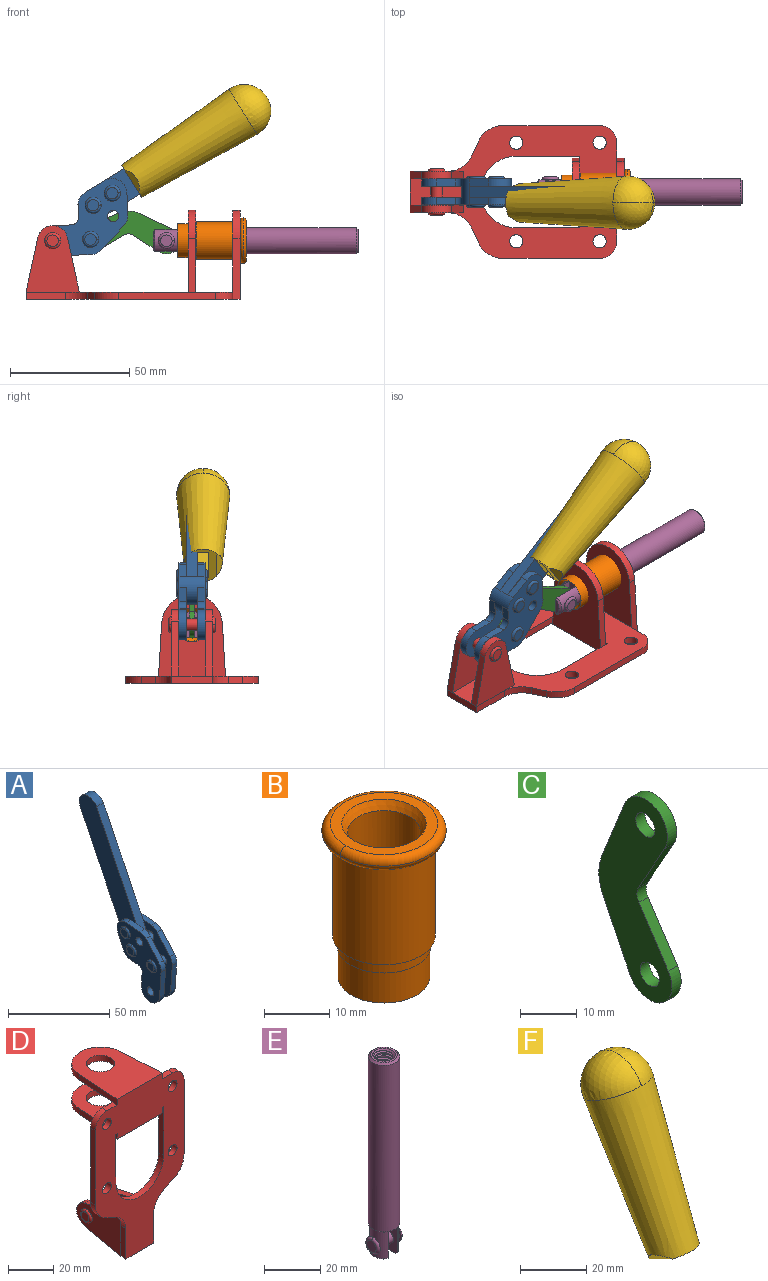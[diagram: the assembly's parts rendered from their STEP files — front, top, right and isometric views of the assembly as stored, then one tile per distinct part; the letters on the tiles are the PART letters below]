
ASSEMBLY  parts=6 mates=6
PART A: 59 faces, bbox 12.9x60.2x99.6 mm
  f0: torus R=2.39mm, axis (-1,0,0), area 14.9mm2, adj f20,f43,f51
  f1: torus R=2.39mm, axis (-1,0,0), area 14.9mm2, adj f19,f42,f51
  f2: torus R=2.39mm, axis (-1,0,0), area 14.9mm2, adj f18,f35,f51
  f3: torus R=2.39mm, axis (-1,0,0), area 14.9mm2, adj f14,f17,f23
  f4: torus R=2.39mm, axis (-1,0,0), area 14.9mm2, adj f13,f16,f23
  f5: torus R=2.39mm, axis (-1,0,0), area 14.9mm2, adj f12,f15,f23
  f6: cylinder r=2.39mm len=4.78mm, axis (1,0,0), area 46.5mm2, adj f48,f50,f51
  f7: cylinder r=2.39mm len=4.78mm, axis (1,0,0), area 46.5mm2, adj f50,f51
  f8: cylinder r=6.35mm len=12.68mm, axis (1,0,0), area 61.8mm2, adj f38,f39,f50,f51
  f9: cylinder r=2.39mm len=4.78mm, axis (-1,0,0), area 70.5mm2, adj f46,f50
  f10: cylinder r=2.39mm len=4.78mm, axis (-1,0,0), area 46.5mm2, adj f23,f45,f46
  f11: cylinder r=2.39mm len=4.78mm, axis (-1,0,0), area 46.5mm2, adj f23,f46
  f12: plane 4.78x4.78mm, normal (1,0,0), area 17.9mm2, adj f5,f15
  f13: plane 4.78x4.78mm, normal (1,0,0), area 17.9mm2, adj f4,f16
  f14: plane 4.78x4.78mm, normal (1,0,0), area 17.9mm2, adj f3,f17
  f15: torus R=2.39mm, axis (-1,0,0), area 14.9mm2, adj f5,f12,f23
  f16: torus R=2.39mm, axis (-1,0,0), area 14.9mm2, adj f4,f13,f23
  f17: torus R=2.39mm, axis (-1,0,0), area 14.9mm2, adj f3,f14,f23
  f18: plane 4.78x4.78mm, normal (-1,0,0), area 17.9mm2, adj f2,f35
  f19: plane 4.78x4.78mm, normal (-1,0,0), area 17.9mm2, adj f1,f42
  f20: plane 4.78x4.78mm, normal (-1,0,0), area 17.9mm2, adj f0,f43
  f21: plane 2.26x0.2mm, normal (1,0,0), area 0.2mm2, adj f31,f44
  f22: plane 2.26x0.2mm, normal (-1,0,0), area 0.2mm2, adj f41,f44
  f23: plane 39.37x30.77mm, normal (1,0,0), area 565.5mm2, adj f3,f4,f5,f10,f11,f15,f16,f17
  f24: cylinder r=6.1mm len=4.15mm, axis (-1,0,0), area 14.7mm2, adj f23,f25,f32,f46
  f25: plane 10.25x9.01mm, normal (0,-0.75,0.66), area 42.3mm2, adj f23,f24,f26,f46
  f26: cylinder r=6.35mm len=4.64mm, axis (-1,0,0), area 15.6mm2, adj f23,f25,f27,f46
  f27: plane 15.84x3.1mm, normal (0,-1,-0.07), area 49.2mm2, adj f23,f26,f28,f46
  f28: cylinder r=6.35mm len=12.68mm, axis (-1,0,0), area 61.8mm2, adj f23,f27,f29,f46
  f29: plane 8.11x3.1mm, normal (0,1,0.07), area 25.2mm2, adj f23,f28,f30,f46
  f30: cylinder r=3.05mm len=3.25mm, axis (-1,0,0), area 14.8mm2, adj f23,f29,f31,f46
  f31: plane 5.99x3.1mm, normal (0,0.07,-1), area 18.6mm2, adj f21,f23,f30,f44,f46
  f32: plane 9.5x3.1mm, normal (0,-0.07,1), area 29.5mm2, adj f23,f24,f33,f46,f47
  f33: cylinder r=6.1mm len=8.63mm, axis (-1,0,0), area 39.1mm2, adj f23,f32,f34,f47
  f34: plane 8.65x3.96mm, normal (0,0.91,-0.42), area 29.5mm2, adj f23,f33,f44,f47
  f35: torus R=2.39mm, axis (-1,0,0), area 14.9mm2, adj f2,f18,f51
  f36: plane 10.25x9.01mm, normal (0,-0.75,0.66), area 42.3mm2, adj f37,f49,f50,f51
  f37: cylinder r=6.35mm len=4.64mm, axis (1,0,0), area 15.6mm2, adj f36,f38,f50,f51
  f38: plane 15.84x3.1mm, normal (0,-1,-0.07), area 49.2mm2, adj f8,f37,f50,f51
  f39: plane 8.11x3.1mm, normal (0,1,0.07), area 25.2mm2, adj f8,f40,f50,f51
  f40: cylinder r=3.05mm len=3.25mm, axis (1,0,0), area 14.8mm2, adj f39,f41,f50,f51
  f41: plane 5.99x3.1mm, normal (0,0.07,-1), area 18.6mm2, adj f22,f40,f44,f50,f51
  f42: torus R=2.39mm, axis (-1,0,0), area 14.9mm2, adj f1,f19,f51
  f43: torus R=2.39mm, axis (-1,0,0), area 14.9mm2, adj f0,f20,f51
  f44: cylinder r=6.35mm len=12.12mm, axis (-1,0,0), area 128.9mm2, adj f21,f22,f23,f31,f34,f41,f46,f47
  f45: plane 2.65x1.35mm, normal (1,0,0), area 1mm2, adj f10,f55
  f46: plane 39.08x20.42mm, normal (-1,0,0), area 412.5mm2, adj f9,f10,f11,f24,f25,f26,f27,f28
  f47: plane 77.62x39.82mm, normal (1,0,0), area 850mm2, adj f32,f33,f34,f44,f53,f54,f55
  f48: plane 2.65x1.35mm, normal (-1,0,0), area 1mm2, adj f6,f55
  f49: cylinder r=6.1mm len=4.15mm, axis (1,0,0), area 14.7mm2, adj f36,f50,f51,f56
  f50: plane 39.08x20.42mm, normal (1,0,0), area 412.5mm2, adj f6,f7,f8,f9,f36,f37,f38,f39
  f51: plane 39.37x30.77mm, normal (-1,0,0), area 565.5mm2, adj f0,f1,f2,f6,f7,f8,f35,f36
  f52: plane 8.65x3.96mm, normal (0,0.91,-0.42), area 29.5mm2, adj f44,f51,f57,f58
  f53: plane 68.49x33.4mm, normal (0,0.9,-0.44), area 358.1mm2, adj f44,f47,f54,f58
  f54: cylinder r=6.35mm len=12.06mm, axis (1,0,0), area 93.7mm2, adj f47,f53,f55,f58
  f55: plane 68.49x33.4mm, normal (0,-0.9,0.44), area 358.1mm2, adj f44,f45,f46,f47,f48,f50,f54,f58
  f56: plane 9.5x3.1mm, normal (0,-0.07,1), area 29.5mm2, adj f49,f50,f51,f57,f58
  f57: cylinder r=6.1mm len=8.63mm, axis (1,0,0), area 39.1mm2, adj f51,f52,f56,f58
  f58: plane 77.62x39.82mm, normal (-1,0,0), area 850mm2, adj f44,f52,f53,f54,f55,f56,f57
PART B: 15 faces, bbox 20.6x20.6x28.7 mm
  f0: torus R=8.26mm, axis (0,0,1), area 56.8mm2, adj f1,f10,f12
  f1: torus R=8.26mm, axis (0,0,1), area 56.8mm2, adj f0,f6,f13
  f2: cylinder r=5.59mm len=25.91mm, axis (0,0,1), area 909.6mm2, adj f3,f4
  f3: cone r=6.86mm half-angle=45deg, axis (0,0,-1), area 70.2mm2, adj f2,f14
  f4: cone r=6.47mm half-angle=30deg, axis (0,0,1), area 66.7mm2, adj f2,f13
  f5: cylinder r=7.04mm len=14.07mm, axis (0,0,1), area 252.6mm2, adj f11,f14
  f6: torus R=8.26mm, axis (0,0,1), area 56.8mm2, adj f1,f12,f13
  f7: cylinder r=7.16mm len=14.33mm, axis (0,0,1), area 91.5mm2, adj f9,f11
  f8: cylinder r=7.86mm len=18.42mm, axis (0,0,1), area 909.6mm2, adj f9,f10
  f9: plane 15.72x15.72mm, normal (0,0,-1), area 33mm2, adj f7,f8
  f10: plane 16.51x16.51mm, normal (0,0,-1), area 19.9mm2, adj f0,f8,f12
  f11: plane 14.33x14.33mm, normal (0,0,-1), area 5.7mm2, adj f5,f7
  f12: torus R=8.26mm, axis (0,0,1), area 56.8mm2, adj f0,f6,f10
  f13: plane 16.51x16.51mm, normal (0,0,1), area 82.7mm2, adj f1,f4,f6
  f14: plane 14.07x14.07mm, normal (0,0,-1), area 7.8mm2, adj f3,f5
PART C: 12 faces, bbox 2.3x18.2x42.8 mm
  f0: cylinder r=2.4mm len=4.8mm, axis (1,0,0), area 34.9mm2, adj f4,f11
  f1: cylinder r=10.41mm len=8.47mm, axis (1,0,0), area 20.2mm2, adj f4,f9,f10,f11
  f2: cylinder r=3.05mm len=3.16mm, axis (1,0,0), area 7.7mm2, adj f4,f6,f7,f11
  f3: cylinder r=2.4mm len=4.8mm, axis (1,0,0), area 34.9mm2, adj f4,f11
  f4: plane 42.81x18.23mm, normal (-1,0,0), area 414.1mm2, adj f0,f1,f2,f3,f5,f6,f7,f8
  f5: cylinder r=5.54mm len=10.67mm, axis (1,0,0), area 41.8mm2, adj f4,f6,f10,f11
  f6: plane 11.66x6.53mm, normal (0,-0.87,-0.49), area 30.9mm2, adj f2,f4,f5,f11
  f7: plane 11.17x7.33mm, normal (0,-0.84,0.55), area 30.9mm2, adj f2,f4,f8,f11
  f8: cylinder r=5.54mm len=10.51mm, axis (1,0,0), area 41.8mm2, adj f4,f7,f9,f11
  f9: plane 13.67x6.67mm, normal (0,0.9,-0.44), area 35.1mm2, adj f1,f4,f8,f11
  f10: plane 14.1x5.7mm, normal (0,0.93,0.37), area 35.1mm2, adj f1,f4,f5,f11
  f11: plane 42.81x18.23mm, normal (1,0,0), area 414.1mm2, adj f0,f1,f2,f3,f5,f6,f7,f8
PART D: 55 faces, bbox 55.7x37.4x89.8 mm
  f0: torus R=2.41mm, axis (-1,0,0), area 15mm2, adj f11,f15,f25
  f1: torus R=2.41mm, axis (-1,0,0), area 15mm2, adj f10,f12,f22
  f2: cylinder r=2.78mm len=5.56mm, axis (0,-1,0), area 54.2mm2, adj f30,f54
  f3: cylinder r=14.99mm len=29.97mm, axis (0,-1,0), area 145.9mm2, adj f30,f49,f53,f54
  f4: cylinder r=2.78mm len=5.56mm, axis (0,-1,0), area 54.2mm2, adj f30,f54
  f5: cylinder r=2.78mm len=5.56mm, axis (0,-1,0), area 54.2mm2, adj f30,f54
  f6: cylinder r=2.78mm len=5.56mm, axis (0,-1,0), area 54.2mm2, adj f30,f54
  f7: cylinder r=6.35mm len=12.7mm, axis (0,0,1), area 123.6mm2, adj f27,f51
  f8: cylinder r=6.35mm len=12.7mm, axis (0,0,-1), area 124.7mm2, adj f21,f35
  f9: cylinder r=2.41mm len=11.18mm, axis (-1,0,0), area 169.4mm2, adj f16,f19
  f10: plane 4.83x4.83mm, normal (1,0,0), area 18.3mm2, adj f1,f12
  f11: plane 4.83x4.83mm, normal (-1,0,0), area 18.3mm2, adj f0,f15
  f12: torus R=2.41mm, axis (-1,0,0), area 15mm2, adj f1,f10,f22
  f13: cylinder r=6.35mm len=12.41mm, axis (1,0,0), area 53.4mm2, adj f18,f19,f22,f23
  f14: cylinder r=6.35mm len=12.41mm, axis (-1,0,0), area 53.4mm2, adj f16,f17,f24,f25
  f15: torus R=2.41mm, axis (-1,0,0), area 15mm2, adj f0,f11,f25
  f16: plane 27.86x22.35mm, normal (1,0,0), area 425.4mm2, adj f9,f14,f17,f24,f30
  f17: plane 22.86x4.97mm, normal (0,0.21,0.98), area 72.5mm2, adj f14,f16,f25,f30
  f18: plane 22.86x4.97mm, normal (0,0.21,0.98), area 72.5mm2, adj f13,f19,f22,f30
  f19: plane 27.86x22.35mm, normal (-1,0,0), area 425.4mm2, adj f9,f13,f18,f23,f30
  f20: cylinder r=12.7mm len=25.35mm, axis (0,0,-1), area 119.8mm2, adj f21,f34,f35,f36
  f21: plane 34.21x28.07mm, normal (0,0,-1), area 702.4mm2, adj f8,f20,f30,f34,f36
  f22: plane 27.96x22.45mm, normal (1,0,0), area 407.2mm2, adj f1,f12,f13,f18,f23,f30,f42,f43
  f23: plane 22.86x4.97mm, normal (0,0.21,-0.98), area 72.5mm2, adj f13,f19,f22,f44
  f24: plane 22.86x4.97mm, normal (0,0.21,-0.98), area 72.5mm2, adj f14,f16,f25,f44
  f25: plane 27.86x22.35mm, normal (-1,0,0), area 407.1mm2, adj f0,f14,f15,f17,f24,f30,f45,f46
  f26: plane 3.1x0.95mm, normal (0,0,-1), area 2.7mm2, adj f30,f49,f50,f54
  f27: plane 34.21x28.07mm, normal (0,0,1), area 702.4mm2, adj f7,f28,f30,f50,f52
  f28: cylinder r=12.7mm len=25.35mm, axis (0,0,1), area 118.8mm2, adj f27,f50,f51,f52
  f29: plane 3.1x0.95mm, normal (0,0,-1), area 2.7mm2, adj f30,f52,f53,f54
  f30: plane 86.54x55.63mm, normal (0,1,0), area 2362.9mm2, adj f2,f3,f4,f5,f6,f16,f17,f18
  f31: plane 40.56x3.1mm, normal (-1,0,0), area 125.7mm2, adj f30,f32,f48,f54
  f32: cylinder r=7.11mm len=7.11mm, axis (0,-1,0), area 34.6mm2, adj f30,f31,f33,f54
  f33: plane 6.67x3.1mm, normal (0,0,1), area 20.4mm2, adj f30,f32,f34,f54
  f34: plane 25.39x3.13mm, normal (-1,0.06,0), area 79.5mm2, adj f20,f21,f33,f35,f54
  f35: plane 37.31x28.45mm, normal (0,0,1), area 789.9mm2, adj f8,f20,f34,f36,f54
  f36: plane 25.39x3.13mm, normal (1,0.06,0), area 79.5mm2, adj f20,f21,f35,f37,f54
  f37: plane 6.67x3.1mm, normal (0,0,1), area 20.4mm2, adj f30,f36,f38,f54
  f38: cylinder r=7.11mm len=7.11mm, axis (0,-1,0), area 34.6mm2, adj f30,f37,f39,f54
  f39: plane 40.56x3.1mm, normal (1,0,0), area 125.7mm2, adj f30,f38,f40,f54
  f40: cylinder r=11.18mm len=10.16mm, axis (0,-1,0), area 39.5mm2, adj f30,f39,f41,f54
  f41: plane 6.09x3.1mm, normal (0.42,0,-0.91), area 20.8mm2, adj f30,f40,f42,f54
  f42: cylinder r=11.18mm len=9.41mm, axis (0,-1,0), area 37.2mm2, adj f22,f30,f41,f43,f54
  f43: plane 16.5x3.1mm, normal (1,0,0), area 51.1mm2, adj f22,f42,f44,f54
  f44: plane 17.37x3.1mm, normal (0,0,-1), area 53.8mm2, adj f23,f24,f30,f43,f45,f54
  f45: plane 16.5x3.1mm, normal (-1,0,0), area 51.1mm2, adj f25,f44,f46,f54
  f46: cylinder r=11.18mm len=9.41mm, axis (0,-1,0), area 37.2mm2, adj f25,f30,f45,f47,f54
  f47: plane 6.09x3.1mm, normal (-0.42,0,-0.91), area 20.8mm2, adj f30,f46,f48,f54
  f48: cylinder r=11.18mm len=10.16mm, axis (0,-1,0), area 39.5mm2, adj f30,f31,f47,f54
  f49: plane 26.54x3.1mm, normal (-1,0,0), area 82.3mm2, adj f3,f26,f30,f54
  f50: plane 25.39x3.1mm, normal (1,0.06,0), area 78.8mm2, adj f26,f27,f28,f51,f54
  f51: plane 37.31x28.45mm, normal (0,0,-1), area 789.9mm2, adj f7,f28,f50,f52,f54
  f52: plane 25.39x3.1mm, normal (-1,0.06,0), area 78.8mm2, adj f27,f28,f29,f51,f54
  f53: plane 26.54x3.1mm, normal (1,0,0), area 82.3mm2, adj f3,f29,f30,f54
  f54: plane 89.66x55.63mm, normal (0,-1,0), area 2678.5mm2, adj f2,f3,f4,f5,f6,f26,f29,f31
PART E: 48 faces, bbox 12.6x11.1x86.1 mm
  f0: torus R=2.41mm, axis (-1,0,0), area 15mm2, adj f30,f32,f34
  f1: torus R=2.41mm, axis (-1,0,0), area 15mm2, adj f29,f31,f33
  f2: cylinder r=5.54mm len=72.39mm, axis (0,0,1), area 2518.5mm2, adj f3,f4,f42,f43
  f3: cone r=5.54mm half-angle=45deg, axis (0,0,1), area 7.6mm2, adj f2,f5,f41
  f4: cone r=5.54mm half-angle=45deg, axis (0,0,-1), area 34.9mm2, adj f2,f39
  f5: cylinder r=5.08mm len=11.48mm, axis (0,0,1), area 108.3mm2, adj f3,f7,f8,f41
  f6: cylinder r=2.41mm len=4.83mm, axis (-1,0,0), area 71.2mm2, adj f40,f41
  f7: cylinder r=2.41mm len=4.83mm, axis (-1,0,0), area 7.6mm2, adj f5,f34
  f8: cone r=5.08mm half-angle=45deg, axis (0,0,1), area 10.6mm2, adj f5,f37,f41
  f9: cone r=3.98mm half-angle=45deg, axis (0,0,1), area 17.6mm2, adj f27,f39,f45,f46,f47
  f10: cylinder r=2.41mm len=4.83mm, axis (-1,0,0), area 7.6mm2, adj f33,f38
  f11: cylinder r=3.2mm len=6.4mm, axis (0,0,1), area 78.4mm2, adj f12,f28,f44,f45,f47
  f12: cylinder r=3.2mm len=6.4mm, axis (0,0,1), area 10.5mm2, adj f11,f13,f45,f47
  f13: cylinder r=3.2mm len=6.4mm, axis (0,0,1), area 10.5mm2, adj f12,f14,f45,f47
  f14: cylinder r=3.2mm len=6.4mm, axis (0,0,1), area 10.5mm2, adj f13,f15,f45,f47
  f15: cylinder r=3.2mm len=6.4mm, axis (0,0,1), area 10.5mm2, adj f14,f16,f45,f47
  f16: cylinder r=3.2mm len=6.4mm, axis (0,0,1), area 10.5mm2, adj f15,f17,f45,f47
  f17: cylinder r=3.2mm len=6.4mm, axis (0,0,1), area 10.5mm2, adj f16,f18,f45,f47
  f18: cylinder r=3.2mm len=6.4mm, axis (0,0,1), area 10.5mm2, adj f17,f19,f45,f47
  f19: cylinder r=3.2mm len=6.4mm, axis (0,0,1), area 10.5mm2, adj f18,f20,f45,f47
  f20: cylinder r=3.2mm len=6.4mm, axis (0,0,1), area 10.5mm2, adj f19,f21,f45,f47
  f21: cylinder r=3.2mm len=6.4mm, axis (0,0,1), area 10.5mm2, adj f20,f22,f45,f47
  f22: cylinder r=3.2mm len=6.4mm, axis (0,0,1), area 10.5mm2, adj f21,f23,f45,f47
  f23: cylinder r=3.2mm len=6.4mm, axis (0,0,1), area 10.5mm2, adj f22,f24,f45,f47
  f24: cylinder r=3.2mm len=6.4mm, axis (0,0,1), area 10.5mm2, adj f23,f25,f45,f47
  f25: cylinder r=3.2mm len=6.4mm, axis (0,0,1), area 10.5mm2, adj f24,f26,f45,f47
  f26: cylinder r=3.2mm len=6.4mm, axis (0,0,1), area 10.5mm2, adj f25,f27,f45,f47
  f27: cylinder r=3.2mm len=6.4mm, axis (0,0,1), area 7.4mm2, adj f9,f26,f45,f47
  f28: cone r=3.2mm half-angle=60deg, axis (0,0,1), area 37.2mm2, adj f11
  f29: plane 4.83x4.83mm, normal (-1,0,0), area 18.3mm2, adj f1,f31
  f30: plane 4.83x4.83mm, normal (1,0,0), area 18.3mm2, adj f0,f32
  f31: torus R=2.41mm, axis (-1,0,0), area 15mm2, adj f1,f29,f33
  f32: torus R=2.41mm, axis (-1,0,0), area 15mm2, adj f0,f30,f34
  f33: plane 6.83x6.83mm, normal (1,0,0), area 18.3mm2, adj f1,f10,f31
  f34: plane 6.83x6.83mm, normal (-1,0,0), area 18.3mm2, adj f0,f7,f32
  f35: cone r=5.08mm half-angle=45deg, axis (0,0,1), area 10.6mm2, adj f36,f38,f40
  f36: plane 7.25x1.97mm, normal (0,0,-1), area 10mm2, adj f35,f40
  f37: plane 7.25x1.97mm, normal (0,0,-1), area 10mm2, adj f8,f41
  f38: cylinder r=5.08mm len=11.48mm, axis (0,0,1), area 108.3mm2, adj f10,f35,f40,f42
  f39: plane 9.55x9.55mm, normal (0,0,1), area 22mm2, adj f4,f9
  f40: plane 12.76x10.09mm, normal (1,0,0), area 95.7mm2, adj f6,f35,f36,f38,f42,f43
  f41: plane 12.76x10.09mm, normal (-1,0,0), area 95.7mm2, adj f3,f5,f6,f8,f37,f43
  f42: cone r=5.54mm half-angle=45deg, axis (0,0,1), area 7.6mm2, adj f2,f38,f40
  f43: plane 11.07x4.7mm, normal (0,0,-1), area 50.4mm2, adj f2,f40,f41
  f44: plane 0.89x0.62mm, normal (-1,0,0), area 0.3mm2, adj f11,f45,f46,f47
  f45: bspline ~24.8x7.63mm, area 266.6mm2, adj f9,f11,f12,f13,f14,f15,f16,f17
  f46: bspline ~24.87x7.63mm, area 73.6mm2, adj f9,f44,f45,f47
  f47: bspline ~24.98x7.63mm, area 272.5mm2, adj f9,f11,f12,f13,f14,f15,f16,f17
PART F: 11 faces, bbox 22.3x42.6x64.5 mm
  f0: sphere r=11.13mm, area 411.4mm2, adj f1,f8
  f1: cone r=11.11mm half-angle=3.3deg, axis (0,0.44,0.9), area 3251.8mm2, adj f0,f7,f8,f9,f10
  f2: cylinder r=6.16mm len=11.7mm, axis (1,0,0), area 89.5mm2, adj f3,f4,f5,f6
  f3: plane 60.23x36.75mm, normal (-1,0,0), area 763.6mm2, adj f2,f4,f6,f10
  f4: plane 51.37x25.05mm, normal (0,0.9,-0.44), area 264.2mm2, adj f2,f3,f5,f10
  f5: plane 60.23x36.75mm, normal (1,0,0), area 763.6mm2, adj f2,f4,f6,f10
  f6: plane 51.37x25.05mm, normal (0,-0.9,0.44), area 264.2mm2, adj f2,f3,f5,f10
  f7: plane 9.95x5.95mm, normal (0.71,-0.31,-0.64), area 25.8mm2, adj f1,f10
  f8: sphere r=11.13mm, area 411.4mm2, adj f0,f1
  f9: plane 9.95x5.95mm, normal (-0.71,-0.31,-0.64), area 25.8mm2, adj f1,f10
  f10: plane 14.27x11.38mm, normal (0,-0.44,-0.9), area 106.7mm2, adj f1,f3,f4,f5,f6,f7,f9
PLACE A rot(axis=(0.56,0.56,0.62),116.6deg) t=(2.38,0,3.45)mm
PLACE B rot(axis=(0,1,0),90deg) t=(0,-24.61,24.61)mm
PLACE C rot(axis=(0.58,-0.58,-0.57),120.6deg) t=(-0.31,0,0.82)mm
PLACE D rot(axis=(0.58,0.58,0.58),120deg) t=(0,0,0)mm fixed
PLACE E rot(axis=(0.58,0.58,0.58),120deg) t=(0.04,0,0)mm
PLACE F rot(axis=(0.56,0.56,0.62),116.6deg) t=(2.38,-4.66,3.45)mm
MATE revolute A.f7 <-> D.f0  axis (0,-1,0) through (-32.09,0,24.61)mm
MATE fastened B.f0 <-> D.f7  axis (-1,0,0) through (46.39,0,24.61)mm
MATE revolute C.f3 <-> E.f6  axis (0,-1,0) through (15.52,0,24.61)mm
MATE slider E.f2 <-> D.f7  axis (1,0,0) through (58.83,0,24.61)mm
MATE fastened F.f2 <-> A.f54  axis (0,-1,0) through (49.5,-2.35,79.78)mm
MATE revolute C.f5 <-> A.f4  axis (0,-1,0) through (-16.23,0,25.15)mm
